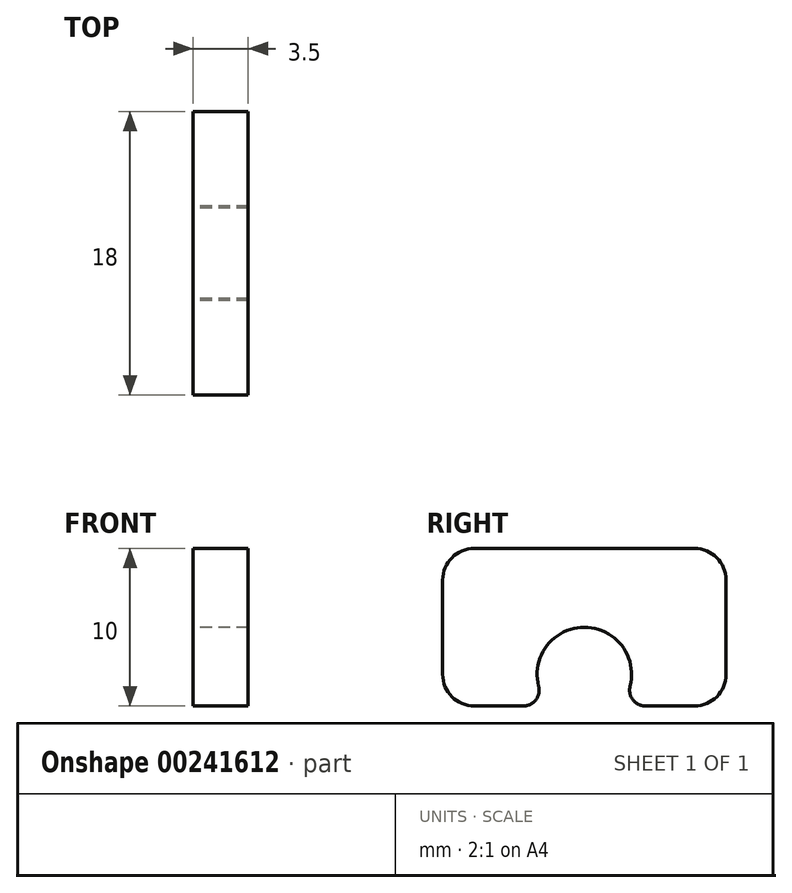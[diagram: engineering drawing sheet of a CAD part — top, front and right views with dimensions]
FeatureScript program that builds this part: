
annotation { "Feature Type Name" : "Feature", "Feature Type Description" : "" }
export const myFeature = defineFeature(function(context is Context, id is Id, definition is map)
    precondition{}
    {
        {
            var Q0;
            Q0=qCreatedBy(makeId("Right.planeOp"),FACE);
            var sketch = newSketch(context, id + "F0", { "sketchPlane" : qUnion([Q0])});
            skLineSegment(sketch, "E0.bottom", {"start": v(-7, 5) * mm, "end": v(7, 5) * mm});
            skLineSegment(sketch, "E0.top", {"start": v(-7, -5) * mm, "end": v(-3.87, -5) * mm});
            skLineSegment(sketch, "E0.left", {"start": v(-9, 3) * mm, "end": v(-9, -3) * mm});
            skLineSegment(sketch, "E0.right", {"start": v(9, 3) * mm, "end": v(9, -3) * mm});
            skPoint(sketch, "E0.middle", {"position": v(0, 0) * mm});
            skArc(sketch, "E1", {"start": v(2.9, -3.75) * mm, "mid": v(0, 0) * mm, "end": v(-2.9, -3.75) * mm});
            skLineSegment(sketch, "E2.trimOffspring", {"start": v(3.87, -5) * mm, "end": v(7, -5) * mm});
            skPoint(sketch, "E3.visualSharp", {"position": v(2.24, -5) * mm});
            skArc(sketch, "E3.filletArc", {"start": v(2.9, -3.75) * mm, "mid": v(3.08, -4.61) * mm, "end": v(3.87, -5) * mm});
            skPoint(sketch, "E4.visualSharp", {"position": v(-2.24, -5) * mm});
            skArc(sketch, "E4.filletArc", {"start": v(-3.87, -5) * mm, "mid": v(-3.08, -4.61) * mm, "end": v(-2.9, -3.75) * mm});
            skPoint(sketch, "E5.visualSharp", {"position": v(-9, 5) * mm});
            skArc(sketch, "E5.filletArc", {"start": v(-7, 5) * mm, "mid": v(-8.41, 4.41) * mm, "end": v(-9, 3) * mm});
            skPoint(sketch, "E6.visualSharp", {"position": v(-9, -5) * mm});
            skArc(sketch, "E6.filletArc", {"start": v(-9, -3) * mm, "mid": v(-8.41, -4.41) * mm, "end": v(-7, -5) * mm});
            skPoint(sketch, "E7.visualSharp", {"position": v(9, -5) * mm});
            skArc(sketch, "E7.filletArc", {"start": v(7, -5) * mm, "mid": v(8.41, -4.41) * mm, "end": v(9, -3) * mm});
            skPoint(sketch, "E8.visualSharp", {"position": v(9, 5) * mm});
            skArc(sketch, "E8.filletArc", {"start": v(9, 3) * mm, "mid": v(8.41, 4.41) * mm, "end": v(7, 5) * mm});
            skSolve(sketch);
        }
        {
            var Q0;
            Q0 = qSketchRegion(id + "F0", true);
            extrude(context, id + "F1", {"entities" : qUnion([Q0]), "depth" : 3.5 * mm});
        }
    });
